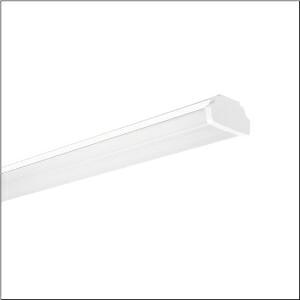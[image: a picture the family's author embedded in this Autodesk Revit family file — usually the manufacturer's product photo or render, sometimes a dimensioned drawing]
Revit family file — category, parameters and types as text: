
# Revit family: modario_r__31_ho_53bm812c1v4105_deab
name_source: partatom
category: Lighting Fixtures
units: mm (PartAtom-declared; Revit-internal decimal feet)

## family parameters
Cut with Voids When Loaded = No
Host = Face
Light Source = No
Part Type = Normal
Room Calculation Point = No
Round Connector Dimension = Use Diameter
Shared = No

## types (1)
- --- (1 x LED, 10520 lm, 63.8 W, 4000K)
    Apparent Load = 64 VA
    CIE Flux Codes = 47 80 95 92 100
    Color Rendering = 80
    Color Temperature = 4000K
    Default Elevation = 1800 mm
    Description = Modario® 31 HO, luminaire insert, of sheet steel, coil coated, white, length: 1.495mm, width: 81mm, height: 82mm, 5x system unit, system units: 299mm, LED rated luminous flux: 10.520lm, light colour: 840, control gear: ON/OFF Multilumen, CLOi, control gear: ECG Multilumen, with plug, 3-pole, with phase selection, mains connection: 220..240V, AC, 50/60Hz, start of lifetime: 64W, end of service life: 73W, through-wiring accessed according to module size, primary optical cover: cover, of PMMA, light emission: direct distribution, primary light characteristic: symmetric, protection rating (complete): IP20, protection rating (LED compartment): IP50, insulation class (complete): insulation class I (protective earthing), certification: CE, ENEC, VDE, UKCA, impact resistance: IK03, permissible ambient temperature for indoor applications: -35..+35°C, corresponds to IFS (International Featured Standards) requirements for safety and quality in the food industry, reducing of maximum allowable ambient temperature of 5°C with ceiling mounting, packaging unit: 1 piece
    Height = 92 mm
    Lamp = 1 x LED
    Lamp Light Flux = 10520 lm
    Lamp Power = 63.8 W
    Lamp count = 1
    Length = 1495 mm
    Luminous efficacy = 165 lm/W
    Manufacturer = Siteco
    ModVariant = No
    Model = 53BM812C1V4105
    Mounting Place = Ceiling
    Mounting Type = Pendant
    Number of Poles = 1
    OnlyDefault = Yes
    Power Factor = 1
    Product Name = Modario® 31 HO
    Product group = luminaire insert
    ProductGroupID = 901
    Protection Class = Protection class I
    Protection Degree = IP 20
    RLX_Detail_Level = 1
    RLX_Emergency_Light_Flux = 0 lm
    RLX_Emergency_Type = 0
    RLX_Emergency_Type_DB = No
    RlxData = <blob elided: 40077 chars, md5=da041716>
    Socket = socket
    Standby Power = 0 W
    System Light Flux = 10520 lm
    System Power = 64 W
    Type Comments = factory setting: luminous flux: 100 % | (A | C | E) | 144 mA
    Type Image = l_1300283.jpg
    URL = http://relux.com
    VarID = @adj_138127
    Voltage = 0 V
    Weight = 0.00 kg
    Width = 81 mm

## geometry (parser evidence)
native form markers: Blend x4, Sweep x13
no freeform markers — native parametric forms only
